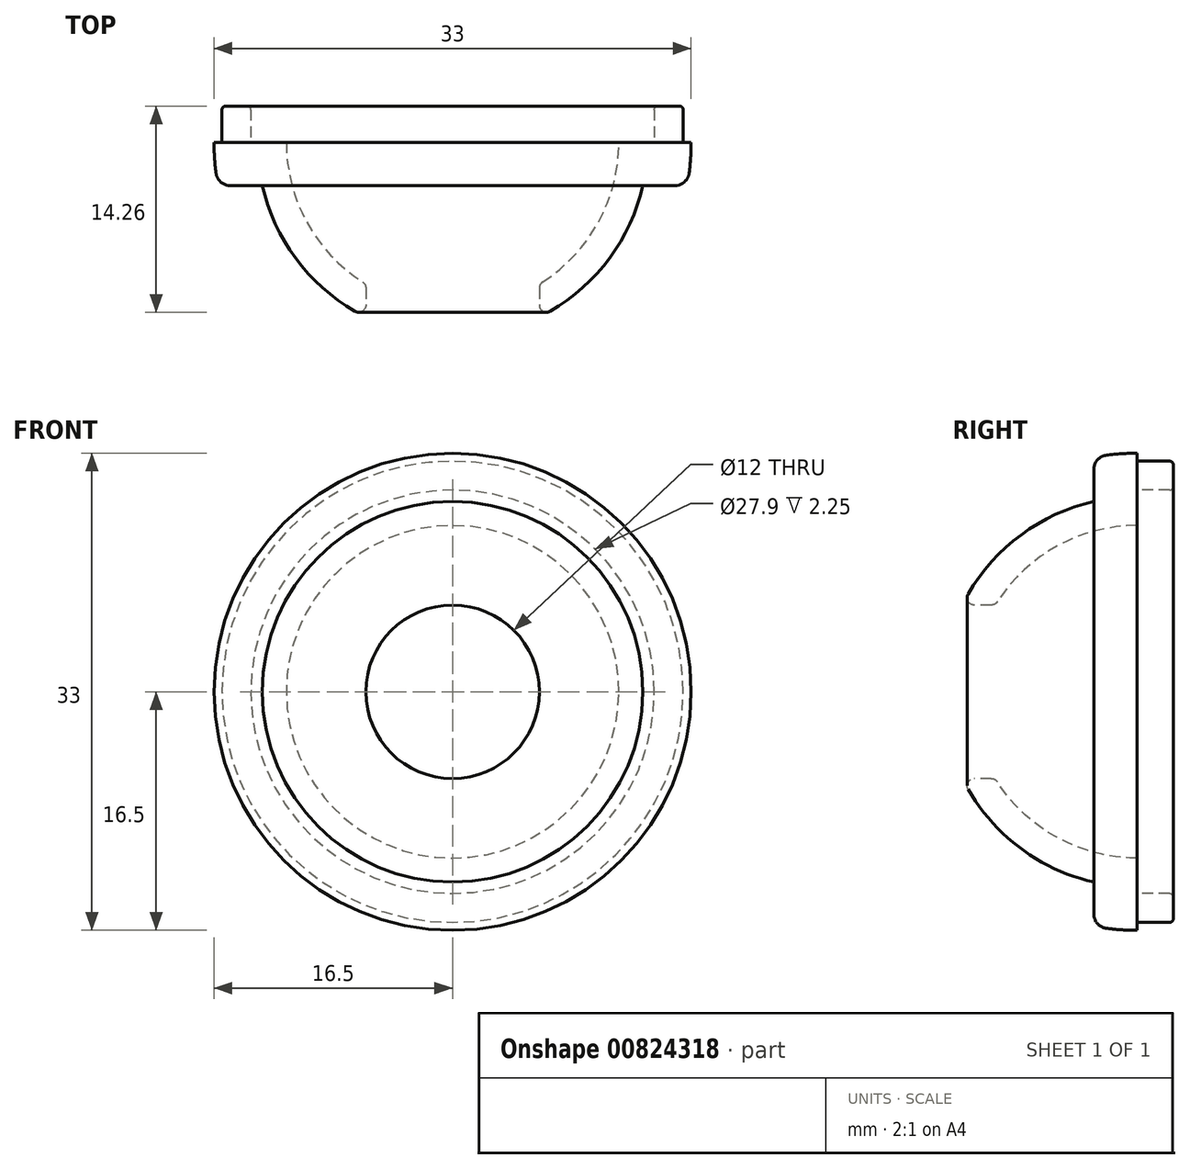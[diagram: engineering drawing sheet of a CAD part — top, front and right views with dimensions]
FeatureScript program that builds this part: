
annotation { "Feature Type Name" : "Feature", "Feature Type Description" : "" }
export const myFeature = defineFeature(function(context is Context, id is Id, definition is map)
    precondition{}
    {
        {
            var Q0;
            Q0=qCreatedBy(makeId("Right.planeOp"),FACE);
            var sketch = newSketch(context, id + "F0", { "sketchPlane" : qUnion([Q0])});
            skLineSegment(sketch, "E0.0", {"start": v(-10.09, 6) * mm, "end": v(-11.26, 6) * mm});
            skArc(sketch, "E1.trimOffspring", {"start": v(0, 11.5) * mm, "mid": v(-5.5, 10.1) * mm, "end": v(-9.67, 6.23) * mm});
            skArc(sketch, "E2.trimOffspring", {"start": v(0, 13.5) * mm, "mid": v(-6.75, 11.7) * mm, "end": v(-11.7, 6.75) * mm});
            skLineSegment(sketch, "E3.trimOffspring", {"start": v(0, 11.5) * mm, "end": v(0, 13.5) * mm});
            skArc(sketch, "E4.filletArc", {"start": v(-11.7, 6.75) * mm, "mid": v(-11.7, 6.25) * mm, "end": v(-11.26, 6) * mm});
            skArc(sketch, "E5.filletArc", {"start": v(-10.09, 6) * mm, "mid": v(-9.85, 6.06) * mm, "end": v(-9.67, 6.23) * mm});
            skArc(sketch, "E6.0", {"start": v(0, 16.5) * mm, "mid": v(-1.07, 16.47) * mm, "end": v(-2.13, 16.36) * mm});
            skLineSegment(sketch, "E7", {"start": v(0, 13.5) * mm, "end": v(0, 16.5) * mm});
            skLineSegment(sketch, "E8.0", {"start": v(-3, 13.16) * mm, "end": v(-3, 15.37) * mm});
            skLineSegment(sketch, "E9", {"start": v(2.25, 15.95) * mm, "end": v(0, 15.95) * mm});
            skPoint(sketch, "E10.visualSharp", {"position": v(-3, 16.22) * mm});
            skArc(sketch, "E10.filletArc", {"start": v(-2.13, 16.36) * mm, "mid": v(-2.75, 16.03) * mm, "end": v(-3, 15.37) * mm});
            skLineSegment(sketch, "E11.0", {"start": v(2.25, 13.95) * mm, "end": v(0, 13.95) * mm});
            skLineSegment(sketch, "E12", {"start": v(2.5, 15.7) * mm, "end": v(2.5, 14.2) * mm});
            skPoint(sketch, "E13.visualSharp", {"position": v(2.5, 15.95) * mm});
            skArc(sketch, "E13.filletArc", {"start": v(2.5, 15.7) * mm, "mid": v(2.43, 15.88) * mm, "end": v(2.25, 15.95) * mm});
            skPoint(sketch, "E14.visualSharp", {"position": v(2.5, 13.95) * mm});
            skArc(sketch, "E14.filletArc", {"start": v(2.25, 13.95) * mm, "mid": v(2.43, 14.02) * mm, "end": v(2.5, 14.2) * mm});
            skLineSegment(sketch, "E15", {"start": v(0, 0) * mm, "end": v(5, 0) * mm});
            skSolve(sketch);
        }
        {
            var Q0;
            {var subQ5=sQuery(id+"F0.wireOp",EDGE,"E6.0");Q0=makeQuery(id+"F0.imprint","IMPRINT",FACE,{"disambiguationData":[TD([[makeQuery(id+"F0.imprint","IMPRINT",EDGE,{"derivedFrom":subQ5}),1.0]])]});}
            var Q1;
            {var subQ0=sQuery(id+"F0.wireOp",EDGE,"E9");Q1=makeQuery(id+"F0.imprint","IMPRINT",FACE,{"disambiguationData":[TD([[makeQuery(id+"F0.imprint","IMPRINT",EDGE,{"derivedFrom":subQ0}),1.0]])]});}
            var Q2;
            Q2=makeQuery(id+"F0.imprint","IMPRINT",FACE,{"disambiguationData":[TD([[makeQuery(id+"F0.imprint","IMPRINT",EDGE,{"derivedFrom":sQuery(id+"F0.wireOp",EDGE,"E0.0")}),-1.0]])]});
            var Q3;
            Q3=sQuery(id+"F0.wireOp",EDGE,"E15");
            revolve(context, id + "F1", {"surfaceOperationType" : NewSurfaceOperationType.NEW, "entities" : qUnion([Q0, Q1, Q2]), "axis" : qUnion([Q3]), "revolveType" : RevolveType.FULL});
        }
    });
